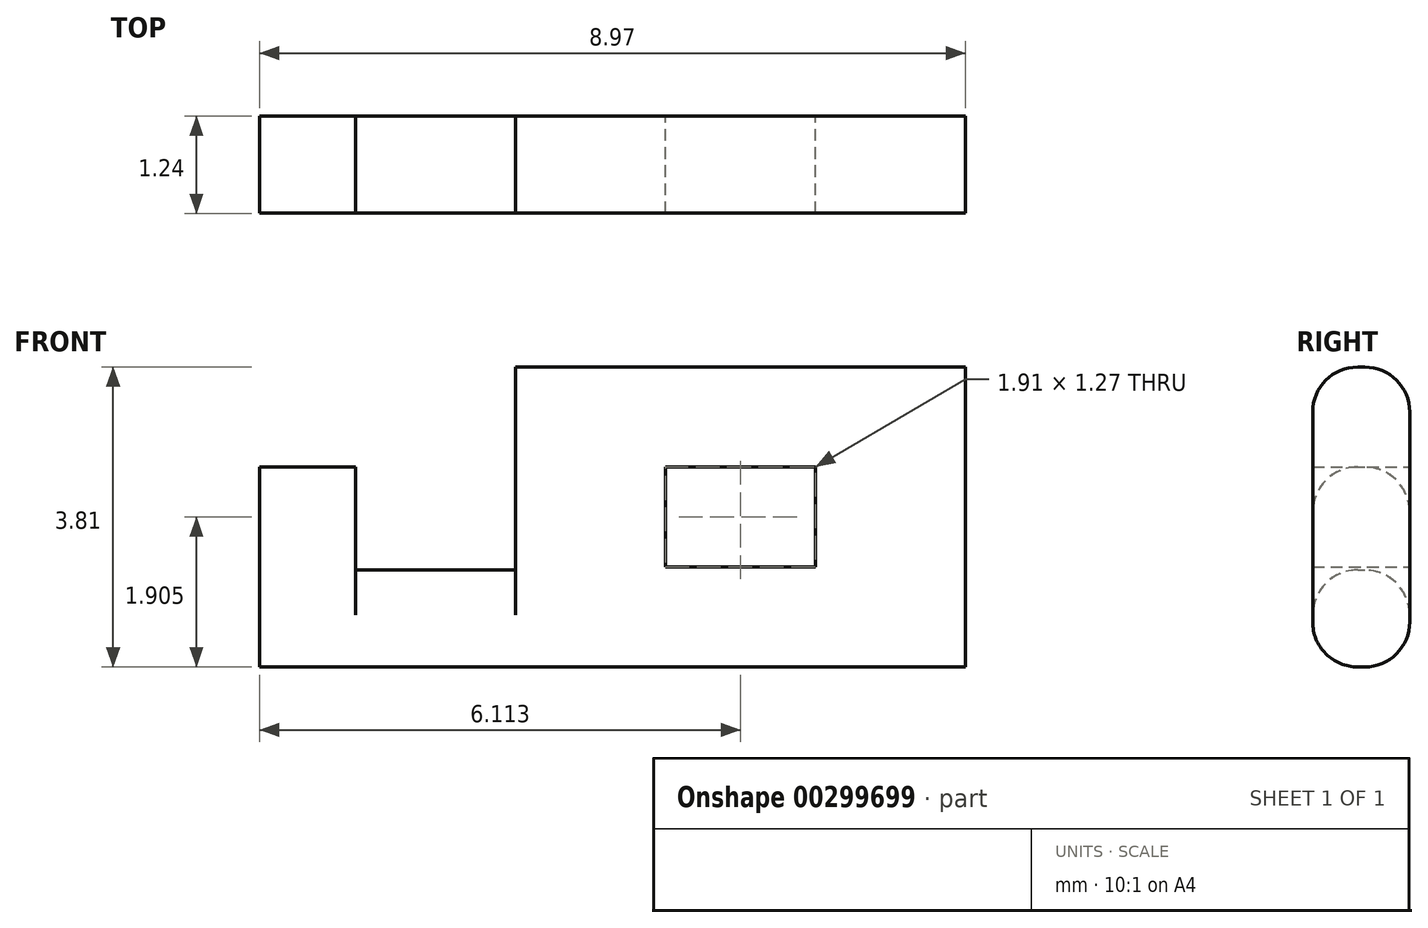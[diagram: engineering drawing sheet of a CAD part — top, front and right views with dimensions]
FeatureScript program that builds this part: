
annotation { "Feature Type Name" : "Feature", "Feature Type Description" : "" }
export const myFeature = defineFeature(function(context is Context, id is Id, definition is map)
    precondition{}
    {
        {
            var Q0;
            Q0=qCreatedBy(makeId("Front.planeOp"),FACE);
            var sketch = newSketch(context, id + "F0", { "sketchPlane" : qUnion([Q0])});
            skLineSegment(sketch, "E0", {"start": v(-7.75, 1.23) * mm, "end": v(-5.71, 1.23) * mm});
            skLineSegment(sketch, "E1", {"start": v(-5.71, 1.23) * mm, "end": v(-5.72, 3.8) * mm});
            skLineSegment(sketch, "E2", {"start": v(-5.72, 3.8) * mm, "end": v(0, 3.8) * mm});
            skLineSegment(sketch, "E3", {"start": v(-8.97, 0) * mm, "end": v(0, 0) * mm});
            skLineSegment(sketch, "E4", {"start": v(0, 0) * mm, "end": v(0, 3.8) * mm});
            skLineSegment(sketch, "E5", {"start": v(-3.81, 2.54) * mm, "end": v(-1.9, 2.54) * mm});
            skLineSegment(sketch, "E6", {"start": v(-1.9, 2.54) * mm, "end": v(-1.9, 1.27) * mm});
            skLineSegment(sketch, "E7", {"start": v(-1.9, 1.27) * mm, "end": v(-3.8, 1.27) * mm});
            skLineSegment(sketch, "E8", {"start": v(-3.8, 1.27) * mm, "end": v(-3.8, 2.54) * mm});
            skLineSegment(sketch, "E9", {"start": v(-8.97, 0) * mm, "end": v(-8.97, 2.54) * mm});
            skLineSegment(sketch, "E10", {"start": v(-8.97, 2.54) * mm, "end": v(-7.75, 2.54) * mm});
            skLineSegment(sketch, "E11", {"start": v(-7.75, 2.54) * mm, "end": v(-7.75, 1.23) * mm});
            skLineSegment(sketch, "E12", {"start": v(-7.75, 1.23) * mm, "end": v(-7.75, 0) * mm});
            skLineSegment(sketch, "E13", {"start": v(-5.71, 1.23) * mm, "end": v(-5.71, 0) * mm});
            skSolve(sketch);
        }
        {
            var Q0;
            {var subQ0=sQuery(id+"F0.wireOp",EDGE,"E9");Q0=makeQuery(id+"F0.imprint","IMPRINT",FACE,{"disambiguationData":[TD([[makeQuery(id+"F0.imprint","IMPRINT",EDGE,{"derivedFrom":subQ0}),-1.0]])]});}
            var Q1;
            Q1=makeQuery(id+"F0.imprint","IMPRINT",FACE,{"disambiguationData":[TD([[makeQuery(id+"F0.imprint","IMPRINT",EDGE,{"derivedFrom":sQuery(id+"F0.wireOp",EDGE,"E1")}),-1.0]])]});
            var Q2;
            Q2=makeQuery(id+"F0.imprint","IMPRINT",FACE,{"disambiguationData":[TD([[makeQuery(id+"F0.imprint","IMPRINT",EDGE,{"derivedFrom":sQuery(id+"F0.wireOp",EDGE,"E0")}),-1.0]])]});
            extrude(context, id + "F1", {"entities" : qUnion([Q0, Q1, Q2]), "endBound" : BoundingType.SYMMETRIC, "depth" : 1.23 * mm});
        }
        {
            var Q0;
            Q0=makeQuery(id+"F1.opExtrude","CAP_EDGE",EDGE,{"disambiguationData":[OSD([sQuery(id+"F0.wireOp",EDGE,"E0")])],"isStart":true});
            var Q1;
            Q1=makeQuery(id+"F1.opExtrude","CAP_EDGE",EDGE,{"disambiguationData":[OSD([sQuery(id+"F0.wireOp",EDGE,"E0")])],"isStart":false});
            var Q2;
            Q2=makeQuery(id+"F1.opExtrude","CAP_EDGE",EDGE,{"disambiguationData":[OSD([sQuery(id+"F0.wireOp",EDGE,"E3")])],"isStart":false});
            var Q3;
            Q3=makeQuery(id+"F1.opExtrude","CAP_EDGE",EDGE,{"disambiguationData":[OSD([sQuery(id+"F0.wireOp",EDGE,"E3")])],"isStart":true});
            var Q4;
            Q4=makeQuery(id+"F1.opExtrude","CAP_EDGE",EDGE,{"disambiguationData":[OSD([sQuery(id+"F0.wireOp",EDGE,"E10")])],"isStart":false});
            var Q5;
            Q5=makeQuery(id+"F1.opExtrude","CAP_EDGE",EDGE,{"disambiguationData":[OSD([sQuery(id+"F0.wireOp",EDGE,"E10")])],"isStart":true});
            var Q6;
            Q6=makeQuery(id+"F1.opExtrude","CAP_EDGE",EDGE,{"disambiguationData":[OSD([sQuery(id+"F0.wireOp",EDGE,"E2")])],"isStart":false});
            var Q7;
            Q7=makeQuery(id+"F1.opExtrude","CAP_EDGE",EDGE,{"disambiguationData":[OSD([sQuery(id+"F0.wireOp",EDGE,"E2")])],"isStart":true});
            fillet(context, id + "F2", {"entities" : qUnion([Q0, Q1, Q2, Q3, Q4, Q5, Q6, Q7]), "radius" : 0.57 * mm, "tangentPropagation" : true, "allowEdgeOverflow" : false});
        }
    });
